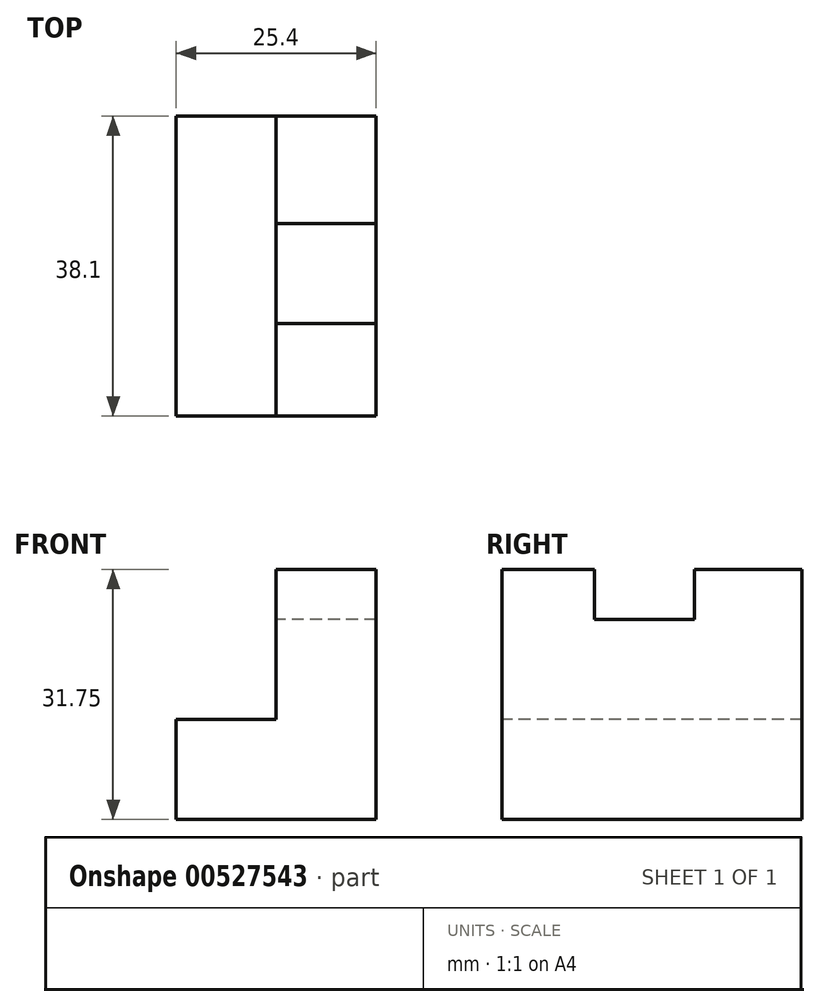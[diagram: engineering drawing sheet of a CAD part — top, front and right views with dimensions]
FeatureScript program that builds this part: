
annotation { "Feature Type Name" : "Feature", "Feature Type Description" : "" }
export const myFeature = defineFeature(function(context is Context, id is Id, definition is map)
    precondition{}
    {
        {
            var Q0;
            Q0=qCreatedBy(makeId("Front.planeOp"),FACE);
            var sketch = newSketch(context, id + "F0", { "sketchPlane" : qUnion([Q0])});
            skLineSegment(sketch, "E0", {"start": v(0, 0) * mm, "end": v(-25.4, 0) * mm});
            skLineSegment(sketch, "E1", {"start": v(0, 0) * mm, "end": v(0, 31.75) * mm});
            skLineSegment(sketch, "E2", {"start": v(-25.4, 0) * mm, "end": v(-25.4, 12.7) * mm});
            skLineSegment(sketch, "E3", {"start": v(-25.4, 12.7) * mm, "end": v(-12.7, 12.7) * mm});
            skLineSegment(sketch, "E4", {"start": v(-12.7, 12.7) * mm, "end": v(-12.7, 31.75) * mm});
            skLineSegment(sketch, "E5", {"start": v(-12.7, 31.75) * mm, "end": v(0, 31.75) * mm});
            skSolve(sketch);
        }
        {
            var Q0;
            Q0=makeQuery(id+"F0.imprint","IMPRINT",FACE,{"disambiguationData":[TD([[makeQuery(id+"F0.imprint","IMPRINT",EDGE,{"derivedFrom":sQuery(id+"F0.wireOp",EDGE,"E0")}),-1.0]])]});
            extrude(context, id + "F1", {"entities" : qUnion([Q0]), "oppositeDirection" : true, "depth" : 38.1 * mm, "offsetDistance" : 25.4 * mm});
        }
        {
            var Q0;
            Q0=makeQuery(id+"F1.opExtrude","SWEPT_FACE",FACE,{"disambiguationData":[OSD([sQuery(id+"F0.wireOp",EDGE,"E4")])]});
            var sketch = newSketch(context, id + "F2", { "sketchPlane" : qUnion([Q0])});
            skLineSegment(sketch, "E6", {"start": v(-24.45, 31.75) * mm, "end": v(-24.45, 25.4) * mm});
            skLineSegment(sketch, "E7", {"start": v(-24.45, 25.4) * mm, "end": v(-11.75, 25.4) * mm});
            skLineSegment(sketch, "E8", {"start": v(-11.75, 25.4) * mm, "end": v(-11.75, 31.75) * mm});
            skSolve(sketch);
        }
        {
            var Q0;
            {var subQ0=sQuery(id+"F2.wireOp",EDGE,"E6");Q0=makeQuery(id+"F2.imprint","IMPRINT",FACE,{"disambiguationData":[TD([[makeQuery(id+"F2.imprint","IMPRINT",EDGE,{"derivedFrom":subQ0}),1.0]])]});}
            extrude(context, id + "F3", {"entities" : qUnion([Q0]), "operationType" : NewBodyOperationType.REMOVE, "oppositeDirection" : true, "depth" : 25.4 * mm, "offsetDistance" : 25.4 * mm});
        }
    });
